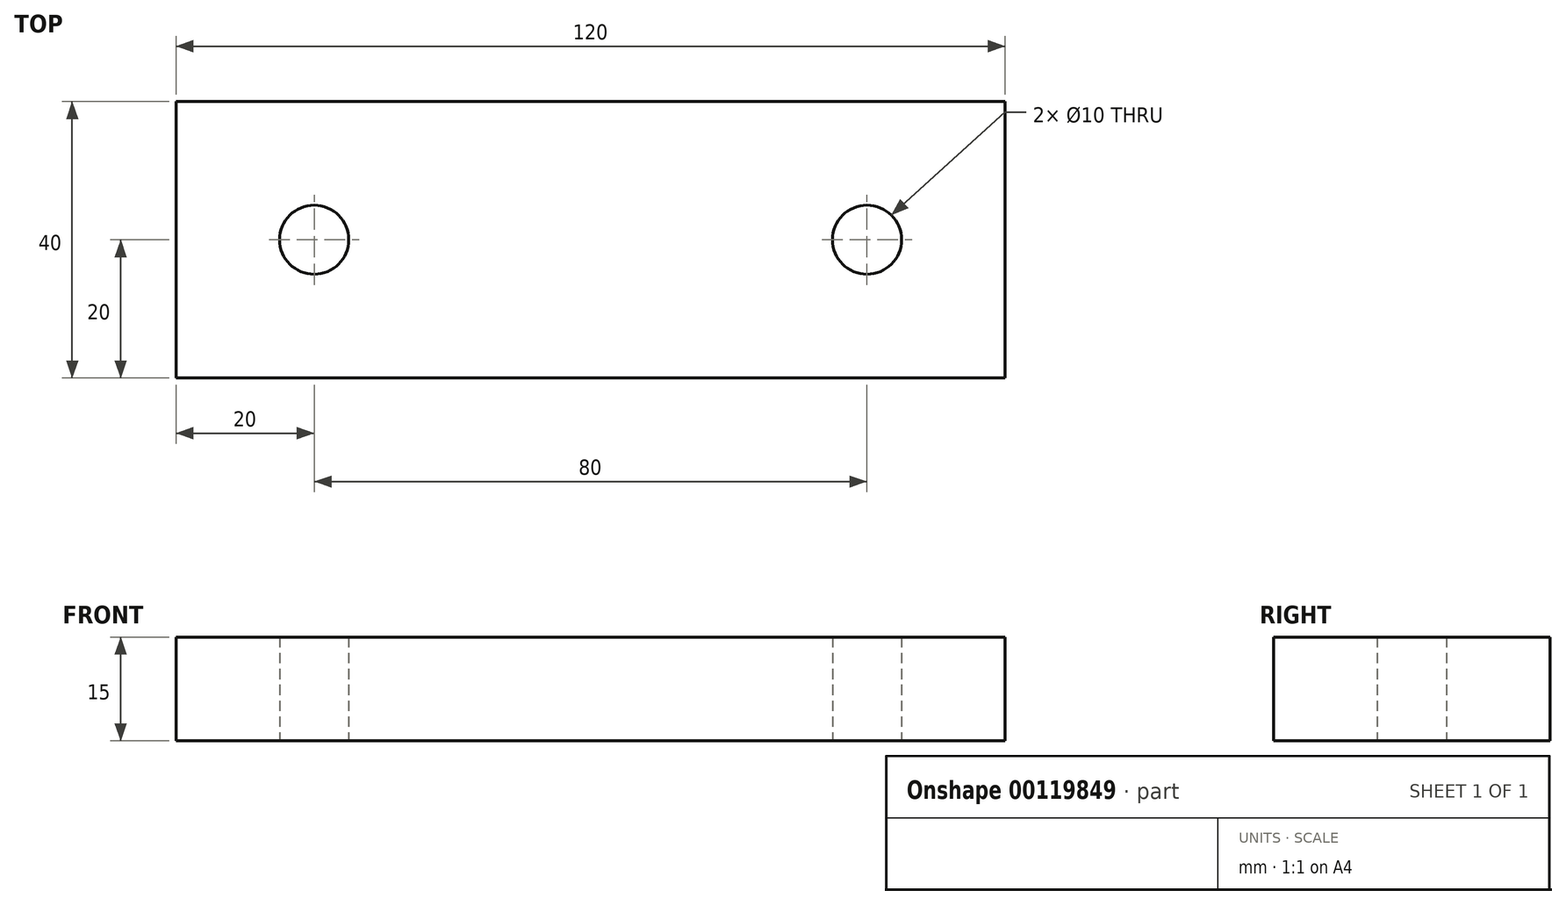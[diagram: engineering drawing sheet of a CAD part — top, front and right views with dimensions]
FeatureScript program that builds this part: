
annotation { "Feature Type Name" : "Feature", "Feature Type Description" : "" }
export const myFeature = defineFeature(function(context is Context, id is Id, definition is map)
    precondition{}
    {
        {
            var Q0;
            Q0=qCreatedBy(makeId("Top.planeOp"),FACE);
            var sketch = newSketch(context, id + "F0", { "sketchPlane" : qUnion([Q0])});
            skLineSegment(sketch, "E0.bottom", {"start": v(-60, -20) * mm, "end": v(60, -20) * mm});
            skLineSegment(sketch, "E0.top", {"start": v(-60, 20) * mm, "end": v(60, 20) * mm});
            skLineSegment(sketch, "E0.left", {"start": v(-60, -20) * mm, "end": v(-60, 20) * mm});
            skLineSegment(sketch, "E0.right", {"start": v(60, -20) * mm, "end": v(60, 20) * mm});
            skCircle(sketch, "E1", {"center": v(40, 0) * mm, "radius": 5 * mm});
            skCircle(sketch, "E2", {"center": v(-40, 0) * mm, "radius": 5 * mm});
            skSolve(sketch);
        }
        {
            var Q0;
            Q0 = qSketchRegion(id + "F0", true);
            extrude(context, id + "F1", {"entities" : qUnion([Q0]), "depth" : 15 * mm});
        }
    });
